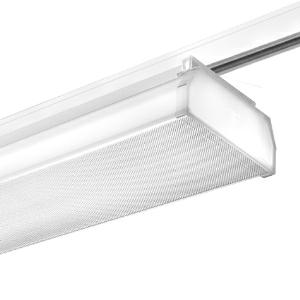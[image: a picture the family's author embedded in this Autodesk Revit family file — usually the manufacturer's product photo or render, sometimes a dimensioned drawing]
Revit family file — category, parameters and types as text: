
# Revit family: 3f_filippi_-_zero_3f_track_3f_filippi_-_45574_-_03f_tk_35w-940_dali_l1204
name_source: partatom
category: Lighting Fixtures
units: mm (PartAtom-declared; Revit-internal decimal feet)

## family parameters
Cut with Voids When Loaded = No
Host = Face
Light Source = No
Part Type = Normal
Room Calculation Point = No
Round Connector Dimension = Use Diameter
Shared = No

## types (1)
- 3F Filippi - Zero 3F Track (1 x LED, 4152 lm, 40 W, 4000 K)
    Apparent Load = 40 VA
    Approval mark = CE
    CIE Flux Codes = 55 84 94 83 100
    Color Rendering = 90
    Color Temperature = 4000 K
    Control Gear = Electronic transformer
    Default Elevation = 1800 mm
    Description = ILLUMINOTECHNICAL
Luminous efficiency 100% (DLOR 83%, ULOR 17%).
Initial luminous flux of the luminaire 4152 lm.
Controlled symmetric distribution.
Installation Interdistance Transv.D = 1.32 x hu - Long.D = 1.30 x hu.
Average luminance <3000 cd/m² for radial angles >65°.
Tabular UGR (CIE 117 - 4H-8H; S=0.25H; 70/50/20): RUG 19.1 - 17.8.
Beam angle: 99° - 100°.
Luminous efficacy 104 lm/W.
Lifetime (L93/B10): 30000 h. (tq+25°C)
Lifetime (L90/B10): 50000 h. (tq+25°C)
Lifetime (L85/B10): 80000 h. (tq+25°C)
Lifetime (L80/B10): 100000 h. (tq+25°C)
Sudden decreased luminous flux after 50000 hours: 0% (C0).
Photobiological safety in compliance with IEC/TR 62778: RG0 risk exempt, (IEC 62471).
In compliance with IEC/EN 62722-2-1 - IEC/EN 62717 standards.

SOURCE
Linear LED module 35W/940.
Energy efficiency class (UE 2019/2020 - UE 2019/2015): E.
CIE 13.3 Colour rendering index: CRI >90 (R9 >50%).
IES TM-30 Fidelity Index: Rf = 92 Rg = 101.
CCT nominal colour temperature 4000 K.
Colour initial tolerance (MacAdam): SDCM 3.

MECHANICAL
Housing in hot-galvanised steel, painted in white polyester.
Diffuser with differentiated geometry, made of transparent methacrylate (PMMA) with microprismatic finish, anti-glare on the flat part and opal on the side.
Anti-glare opal methacrylate (PMMA) filter for brightness uniformity.
Lighting end caps in methacrylate (PMMA) opal.
Supporting mechanical adapter.
Luminaire with limited surface temperature. - D - (EN 60598-2-24)
Dimensions: 1204x119 mm, height 64 mm. Weight 2.62 kg.
IP40 protection degree.
Mechanical strength to impacts IK06 (1 joule).
Glow-wire test resistance 650°C.

ELECTRICAL
Halogen Free DALI-2 DATI (Parts 251, 252, 253), PUSH-DIM, electronic wiring 230V-50/60Hz, power factor 0.95 at full load, THD <25%, constant output current, SELV, class I, 1 driver, 1 DALI addresse.
Power of the luminaire 40 W.
ENEC - CE.
SAFE FLICKER: PstLM=<1 and SVM=<0.4 (IEC TR 61547-1 and IEC TR 63158), to ensure a more comfortable and safe light.
Ambient temperature from 0°C to +25°C.
Temperature class T6 max 85°C.
Truck adapter, 4/6-way.
Relative humidity UR: <85%.

INSTALLATION
Track.

APPLICATIONS
Environments: with VDTs, meeting rooms, offices.
Environments: recreational, transit areas, corridors, schools, stairwells.
Environments where soft diffuse light is required for optimal visual comfort.

LIGHT MANAGEMENT
Recommended minimum setting: 10%.
The luminaire, equipped with (DALI-2 DATI) driver, can be controlled manually with 3F Easy Dim technology or automatically/manually with wired or wireless DALI/D2D control systems.
The D2D driver guarantees interoperability with other devices with the same certification by making the following information available:
Device Data (Part 251), Energy Report (Part 252), Diagnosis & Maintenance (Part 253).
In electrical systems without a regulation system (manual or automatic) and DALI bus, a suitable jumper must be made on the DA-DA terminals of the appliance.

WARNING
Luminaire designed for disposal/recycling at end-of-life.
Replaceable (LED only) light source by a professional. Replaceable control gear by a professional.
    Height = 64 mm
    Lamp = 1 x LED
    Lamp Light Flux = 4152 lm
    Lamp Power = 40 W
    Lamp count = 1
    Length = 1204 mm
    Lifetime = 50000 h
    Luminous efficacy = 104 lm/W
    Manufacturer = 3F Filippi
    ModVariant = No
    Model = 3F Filippi - 45574 - 03F TK 35W-940 DALI L1204
    Mounting Place = Ceiling
    Mounting Type = Rail mounted
    Number of Poles = 1
    OnlyDefault = Yes
    Power Factor = 1
    Product Name = 3F Filippi - Zero 3F Track
    Product group = track mounted spotlight
    ProductGroupID = 12
    Protection Class = Protection class I
    Protection Degree = IP 40
    RLX_Detail_Level = 1
    RLX_Emergency_Light_Flux = 0 lm
    RLX_Emergency_Type = 0
    RLX_Emergency_Type_DB = No
    RlxData = <blob elided: 193273 chars, md5=350a3db3>
    Socket = socket
    Standby Power = 0 W
    System Light Flux = 4152 lm
    System Power = 40 W
    Type Comments = Product without accessories
    Type Image = 3ffilippi_zero_3f_track.jpg
    URL = http://relux.com
    VarID = ---
    Voltage = 0 V
    Weight = 0.00 kg
    Width = 119 mm

## geometry (parser evidence)
native form markers: Blend x4, Sweep x17
no freeform markers — native parametric forms only
